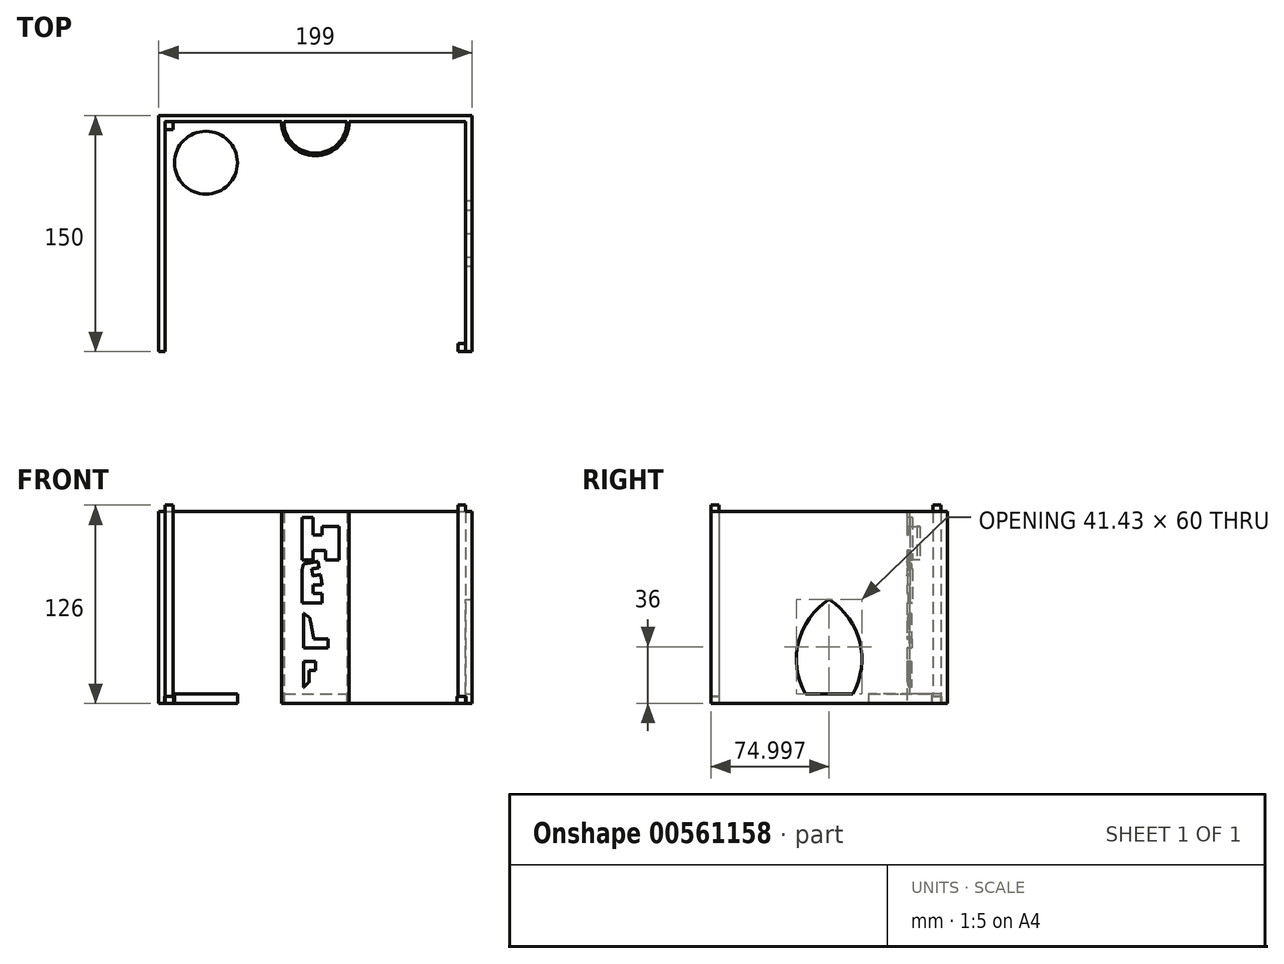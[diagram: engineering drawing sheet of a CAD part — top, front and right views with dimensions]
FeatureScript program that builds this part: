
annotation { "Feature Type Name" : "Feature", "Feature Type Description" : "" }
export const myFeature = defineFeature(function(context is Context, id is Id, definition is map)
    precondition{}
    {
        {
            var Q0;
            Q0=qCreatedBy(makeId("Top.planeOp"),FACE);
            var sketch = newSketch(context, id + "F0", { "sketchPlane" : qUnion([Q0])});
            skLineSegment(sketch, "E0.bottom", {"start": v(-131.47, 174.02) * mm, "end": v(-41.13, 174.02) * mm});
            skLineSegment(sketch, "E0.top", {"start": v(-131.47, 24.02) * mm, "end": v(-122.47, 24.02) * mm});
            skLineSegment(sketch, "E0.right", {"start": v(67.53, 174.02) * mm, "end": v(67.53, 24.02) * mm});
            skLineSegment(sketch, "E1", {"start": v(-131.47, 174.02) * mm, "end": v(-131.47, 24.02) * mm});
            skLineSegment(sketch, "E2.0", {"start": v(-127.47, 170.02) * mm, "end": v(-122.47, 170.02) * mm});
            skLineSegment(sketch, "E3.0", {"start": v(-127.47, 170.02) * mm, "end": v(-127.47, 24.02) * mm});
            skLineSegment(sketch, "E4.0", {"start": v(63.53, 170.02) * mm, "end": v(63.53, 24.02) * mm});
            skLineSegment(sketch, "E5", {"start": v(-19.6, 170.02) * mm, "end": v(63.53, 170.02) * mm});
            skLineSegment(sketch, "E6.top", {"start": v(-127.47, 165.02) * mm, "end": v(-122.47, 165.02) * mm});
            skLineSegment(sketch, "E6.left", {"start": v(-127.47, 170.02) * mm, "end": v(-127.47, 165.02) * mm});
            skLineSegment(sketch, "E6.right", {"start": v(-122.47, 170.02) * mm, "end": v(-122.47, 165.02) * mm});
            skLineSegment(sketch, "E7.bottom", {"start": v(63.53, 170.02) * mm, "end": v(58.53, 170.02) * mm});
            skLineSegment(sketch, "E7.top", {"start": v(63.53, 165.02) * mm, "end": v(58.53, 165.02) * mm});
            skLineSegment(sketch, "E7.left", {"start": v(63.53, 170.02) * mm, "end": v(63.53, 165.02) * mm});
            skLineSegment(sketch, "E7.right", {"start": v(58.53, 170.02) * mm, "end": v(58.53, 165.02) * mm});
            skLineSegment(sketch, "E8.bottom", {"start": v(-127.47, 24.02) * mm, "end": v(-122.47, 24.02) * mm});
            skLineSegment(sketch, "E8.top", {"start": v(-127.47, 29.02) * mm, "end": v(-122.47, 29.02) * mm});
            skLineSegment(sketch, "E8.left", {"start": v(-127.47, 24.02) * mm, "end": v(-127.47, 29.02) * mm});
            skLineSegment(sketch, "E8.right", {"start": v(-122.47, 24.02) * mm, "end": v(-122.47, 29.02) * mm});
            skLineSegment(sketch, "E9.bottom", {"start": v(63.53, 24.02) * mm, "end": v(58.53, 24.02) * mm});
            skLineSegment(sketch, "E9.top", {"start": v(63.53, 29.02) * mm, "end": v(58.53, 29.02) * mm});
            skLineSegment(sketch, "E9.left", {"start": v(63.53, 24.02) * mm, "end": v(63.53, 29.02) * mm});
            skLineSegment(sketch, "E9.right", {"start": v(58.53, 24.02) * mm, "end": v(58.53, 29.02) * mm});
            skPoint(sketch, "E10.centerSnap0", {"position": v(-31.97, 174.02) * mm});
            skLineSegment(sketch, "E11.trimOffspring", {"start": v(-22.8, 174.02) * mm, "end": v(67.53, 174.02) * mm});
            skLineSegment(sketch, "E12.trimOffspring", {"start": v(-21.97, 170.02) * mm, "end": v(-19.6, 170.02) * mm});
            skLineSegment(sketch, "E13", {"start": v(-21.97, 170.02) * mm, "end": v(-122.47, 170.02) * mm});
            skLineSegment(sketch, "E14", {"start": v(-41.13, 174.02) * mm, "end": v(-22.8, 174.02) * mm});
            skPoint(sketch, "E10.center.orphan", {"position": v(-31.97, 170.02) * mm});
            skArc(sketch, "E15", {"start": v(-51.97, 170.02) * mm, "mid": v(-31.97, 150.02) * mm, "end": v(-11.97, 170.02) * mm});
            skArc(sketch, "E16", {"start": v(-53.47, 170.02) * mm, "mid": v(-31.97, 148.52) * mm, "end": v(-10.47, 170.02) * mm});
            skLineSegment(sketch, "E17.trimOffspring", {"start": v(58.53, 24.02) * mm, "end": v(67.53, 24.02) * mm});
            skSolve(sketch);
        }
        {
            var Q0;
            Q0=makeQuery(id+"F0.imprint","IMPRINT",FACE,{"disambiguationData":[TD([[makeQuery(id+"F0.imprint","IMPRINT",EDGE,{"derivedFrom":sQuery(id+"F0.wireOp",EDGE,"E0.bottom")}),-1.0]])]});
            var Q1;
            {var subQ0=sQuery(id+"F0.wireOp",EDGE,"E15");Q1=makeQuery(id+"F0.imprint","IMPRINT",FACE,{"disambiguationData":[TD([[makeQuery(id+"F0.imprint","IMPRINT",EDGE,{"derivedFrom":subQ0}),-1.0]])]});}
            extrude(context, id + "F1", {"entities" : qUnion([Q0, Q1]), "depth" : 122 * mm, "offsetDistance" : 25 * mm});
        }
        {
            var Q0;
            Q0=makeQuery(id+"F0.imprint","IMPRINT",FACE,{"disambiguationData":[TD([[makeQuery(id+"F0.imprint","IMPRINT",EDGE,{"derivedFrom":sQuery(id+"F0.wireOp",EDGE,"E2.0")}),-1.0]])]});
            var Q1;
            Q1=makeQuery(id+"F0.imprint","IMPRINT",FACE,{"disambiguationData":[TD([[makeQuery(id+"F0.imprint","IMPRINT",EDGE,{"derivedFrom":sQuery(id+"F0.wireOp",EDGE,"E7.bottom")}),1.0]])]});
            var Q2;
            Q2=makeQuery(id+"F0.imprint","IMPRINT",FACE,{"disambiguationData":[TD([[makeQuery(id+"F0.imprint","IMPRINT",EDGE,{"derivedFrom":sQuery(id+"F0.wireOp",EDGE,"E9.top")}),1.0]])]});
            var Q3;
            Q3=makeQuery(id+"F0.imprint","IMPRINT",FACE,{"disambiguationData":[TD([[makeQuery(id+"F0.imprint","IMPRINT",EDGE,{"derivedFrom":sQuery(id+"F0.wireOp",EDGE,"E8.bottom")}),1.0]])]});
            extrude(context, id + "F2", {"entities" : qUnion([Q0, Q1, Q2, Q3]), "operationType" : NewBodyOperationType.ADD, "depth" : 126 * mm, "offsetDistance" : 25 * mm});
        }
        {
            var Q0;
            Q0=makeQuery(id+"F0.imprint","IMPRINT",FACE,{"disambiguationData":[TD([[makeQuery(id+"F0.imprint","IMPRINT",EDGE,{"derivedFrom":sQuery(id+"F0.wireOp",EDGE,"E0.bottom")}),-1.0]])]});
            var sketch = newSketch(context, id + "F3", { "sketchPlane" : qUnion([Q0])});
            skLineSegment(sketch, "E18.bottom", {"start": v(67.54, 24.02) * mm, "end": v(-131.47, 24.02) * mm});
            skLineSegment(sketch, "E18.top", {"start": v(67.54, 174.02) * mm, "end": v(-131.47, 174.02) * mm});
            skLineSegment(sketch, "E18.left", {"start": v(67.54, 24.02) * mm, "end": v(67.54, 174.02) * mm});
            skLineSegment(sketch, "E18.right", {"start": v(-131.47, 24.02) * mm, "end": v(-131.47, 174.02) * mm});
            skLineSegment(sketch, "E19", {"start": v(-131.47, 174.02) * mm, "end": v(-101.47, 174.02) * mm});
            skCircle(sketch, "E20", {"center": v(-101.47, 144.02) * mm, "radius": 20 * mm});
            skLineSegment(sketch, "E21", {"start": v(-51.96, 170.02) * mm, "end": v(-11.96, 170.02) * mm});
            skArc(sketch, "E22", {"start": v(-51.96, 170.02) * mm, "mid": v(-31.96, 150.02) * mm, "end": v(-11.96, 170.02) * mm});
            skSolve(sketch);
        }
        {
            var Q0;
            Q0 = qSketchRegion(id + "F3", true);
            extrude(context, id + "F4", {"entities" : qUnion([Q0]), "operationType" : NewBodyOperationType.ADD, "depth" : 6 * mm, "offsetDistance" : 25 * mm});
        }
        {
            var Q0;
            Q0=makeQuery(id+"F1.opExtrude","SWEPT_FACE",FACE,{"disambiguationData":[OSD([sQuery(id+"F0.wireOp",EDGE,"E0.right")])]});
            var sketch = newSketch(context, id + "F5", { "sketchPlane" : qUnion([Q0])});
            skPoint(sketch, "E23.endSnap0", {"position": v(99.02, 0) * mm});
            skLineSegment(sketch, "E24", {"start": v(99.02, 6) * mm, "end": v(114.02, 6) * mm});
            skLineSegment(sketch, "E25.MirrorCS", {"start": v(99.02, 6) * mm, "end": v(84.02, 6) * mm});
            skArc(sketch, "E26", {"start": v(114.02, 6) * mm, "mid": v(118.46, 38.99) * mm, "end": v(99.02, 66) * mm});
            skArc(sketch, "E27.MirrorCS", {"start": v(84.02, 6) * mm, "mid": v(79.58, 38.99) * mm, "end": v(99.02, 66) * mm});
            skPoint(sketch, "E23.start.orphan", {"position": v(99.02, 0) * mm});
            skSolve(sketch);
        }
        {
            var Q0;
            Q0=makeQuery(id+"F5.imprint","IMPRINT",FACE,{"disambiguationData":[TD([[makeQuery(id+"F5.imprint","IMPRINT",EDGE,{"derivedFrom":sQuery(id+"F5.wireOp",EDGE,"E24")}),1.0]])]});
            extrude(context, id + "F6", {"entities" : qUnion([Q0]), "operationType" : NewBodyOperationType.REMOVE, "oppositeDirection" : true, "depth" : 4 * mm, "offsetDistance" : 25 * mm});
        }
        {
            var Q0;
            {var subQ0=sQuery(id+"F0.wireOp",EDGE,"E17.trimOffspring");var subQ1=sQuery(id+"F0.wireOp",EDGE,"E9.left");var subQ2=sQuery(id+"F0.wireOp",EDGE,"E8.left");var subQ3=sQuery(id+"F0.wireOp",EDGE,"E7.left");var subQ4=sQuery(id+"F0.wireOp",EDGE,"E7.bottom");var subQ5=sQuery(id+"F0.wireOp",EDGE,"E6.left");var subQ6=sQuery(id+"F0.wireOp",EDGE,"E2.0");Q0=makeQuery(id+"F4.boolean.opBoolean","MERGE",FACE,{"derivedFrom":[makeQuery(id+"F2.boolean.opBoolean","MERGE",FACE,{"derivedFrom":[makeQuery(id+"F1.opExtrude","CAP_FACE",FACE,{"disambiguationData":[OSD([sQuery(id+"F0.wireOp",EDGE,"E0.bottom"),sQuery(id+"F0.wireOp",EDGE,"E0.top"),sQuery(id+"F0.wireOp",EDGE,"E0.right"),sQuery(id+"F0.wireOp",EDGE,"E1"),sQuery(id+"F0.wireOp",EDGE,"E3.0"),sQuery(id+"F0.wireOp",EDGE,"E4.0"),sQuery(id+"F0.wireOp",EDGE,"E5"),subQ6,subQ5,subQ4,subQ3,subQ2,subQ1,sQuery(id+"F0.wireOp",EDGE,"E11.trimOffspring"),sQuery(id+"F0.wireOp",EDGE,"E12.trimOffspring"),sQuery(id+"F0.wireOp",EDGE,"E13"),sQuery(id+"F0.wireOp",EDGE,"E14"),sQuery(id+"F0.wireOp",EDGE,"E15"),sQuery(id+"F0.wireOp",EDGE,"E16"),subQ0])],"isStart":true}),makeQuery(id+"F2.opExtrude","CAP_FACE",FACE,{"disambiguationData":[OSD([subQ6,sQuery(id+"F0.wireOp",EDGE,"E6.top"),subQ5,sQuery(id+"F0.wireOp",EDGE,"E6.right")])],"isStart":true}),makeQuery(id+"F2.opExtrude","CAP_FACE",FACE,{"disambiguationData":[OSD([subQ4,sQuery(id+"F0.wireOp",EDGE,"E7.top"),subQ3,sQuery(id+"F0.wireOp",EDGE,"E7.right")])],"isStart":true}),makeQuery(id+"F2.opExtrude","CAP_FACE",FACE,{"disambiguationData":[OSD([sQuery(id+"F0.wireOp",EDGE,"E8.bottom"),sQuery(id+"F0.wireOp",EDGE,"E8.top"),subQ2,sQuery(id+"F0.wireOp",EDGE,"E8.right")])],"isStart":true}),makeQuery(id+"F2.opExtrude","CAP_FACE",FACE,{"disambiguationData":[OSD([sQuery(id+"F0.wireOp",EDGE,"E9.top"),subQ1,sQuery(id+"F0.wireOp",EDGE,"E9.right"),subQ0])],"isStart":true})]}),makeQuery(id+"F4.opExtrude","CAP_FACE",FACE,{"disambiguationData":[OSD([sQuery(id+"F3.wireOp",EDGE,"E18.bottom"),sQuery(id+"F3.wireOp",EDGE,"E18.top"),sQuery(id+"F3.wireOp",EDGE,"E18.left"),sQuery(id+"F3.wireOp",EDGE,"E18.right"),sQuery(id+"F3.wireOp",EDGE,"E19"),sQuery(id+"F3.wireOp",EDGE,"E20"),sQuery(id+"F3.wireOp",EDGE,"E21"),sQuery(id+"F3.wireOp",EDGE,"E22")])],"isStart":true})]});}
            var sketch = newSketch(context, id + "F7", { "sketchPlane" : qUnion([Q0])});
            skLineSegment(sketch, "E28.bottom", {"start": v(-127.47, -24.02) * mm, "end": v(-122.19, -24.02) * mm});
            skLineSegment(sketch, "E29", {"start": v(-127.72, -24.02) * mm, "end": v(-127.72, -29.32) * mm});
            skLineSegment(sketch, "E30", {"start": v(-127.72, -29.32) * mm, "end": v(-122.19, -29.32) * mm});
            skLineSegment(sketch, "E31", {"start": v(-122.19, -29.32) * mm, "end": v(-122.19, -24.02) * mm});
            skLineSegment(sketch, "E32.bottom", {"start": v(58.53, -24.02) * mm, "end": v(58.28, -24.02) * mm});
            skLineSegment(sketch, "E33.top", {"start": v(58.28, -29.23) * mm, "end": v(63.85, -29.23) * mm});
            skLineSegment(sketch, "E33.left", {"start": v(58.28, -24.02) * mm, "end": v(58.28, -29.23) * mm});
            skLineSegment(sketch, "E33.right", {"start": v(63.85, -24.02) * mm, "end": v(63.85, -29.23) * mm});
            skLineSegment(sketch, "E34.top", {"start": v(63.54, -170.26) * mm, "end": v(63.78, -170.26) * mm});
            skLineSegment(sketch, "E34.right", {"start": v(63.78, -170.02) * mm, "end": v(63.78, -170.26) * mm});
            skLineSegment(sketch, "E35.bottom", {"start": v(63.78, -170.26) * mm, "end": v(58.1, -170.26) * mm});
            skLineSegment(sketch, "E35.top", {"start": v(63.78, -164.76) * mm, "end": v(58.1, -164.76) * mm});
            skLineSegment(sketch, "E35.left", {"start": v(63.78, -170.26) * mm, "end": v(63.78, -164.76) * mm});
            skLineSegment(sketch, "E35.right", {"start": v(58.1, -170.26) * mm, "end": v(58.1, -164.76) * mm});
            skLineSegment(sketch, "E36.top", {"start": v(-127.46, -170.3) * mm, "end": v(-127.71, -170.3) * mm});
            skLineSegment(sketch, "E36.right", {"start": v(-127.71, -170.02) * mm, "end": v(-127.71, -170.3) * mm});
            skLineSegment(sketch, "E37.bottom", {"start": v(-127.71, -170.3) * mm, "end": v(-121.95, -170.3) * mm});
            skLineSegment(sketch, "E37.top", {"start": v(-127.71, -164.76) * mm, "end": v(-121.95, -164.76) * mm});
            skLineSegment(sketch, "E37.left", {"start": v(-127.71, -170.3) * mm, "end": v(-127.71, -164.76) * mm});
            skLineSegment(sketch, "E37.right", {"start": v(-121.95, -170.3) * mm, "end": v(-121.95, -164.76) * mm});
            skLineSegment(sketch, "E38", {"start": v(58.28, -24.02) * mm, "end": v(63.85, -24.02) * mm});
            skPoint(sketch, "E39.orphan", {"position": v(-122.19, -23.76) * mm});
            skLineSegment(sketch, "E40", {"start": v(-127.47, -24.02) * mm, "end": v(-127.72, -24.02) * mm});
            skPoint(sketch, "E41.end.orphan", {"position": v(-127.47, -23.76) * mm});
            skSolve(sketch);
        }
        {
            var Q0;
            Q0 = qSketchRegion(id + "F7", true);
            extrude(context, id + "F8", {"entities" : qUnion([Q0]), "operationType" : NewBodyOperationType.REMOVE, "oppositeDirection" : true, "depth" : 4.5 * mm, "offsetDistance" : 25 * mm});
        }
        {
            var Q0;
            Q0=qCreatedBy(makeId("Front.planeOp"),FACE);
            var sketch = newSketch(context, id + "F9", { "sketchPlane" : qUnion([Q0])});
            skLineSegment(sketch, "E42", {"start": v(-40.33, 105.44) * mm, "end": v(-40.33, 91.16) * mm});
            skLineSegment(sketch, "E43", {"start": v(-40.33, 91.16) * mm, "end": v(-33.59, 91.16) * mm});
            skLineSegment(sketch, "E44", {"start": v(-33.59, 91.16) * mm, "end": v(-33.59, 97.1) * mm});
            skLineSegment(sketch, "E45", {"start": v(-33.59, 97.1) * mm, "end": v(-25.65, 97.1) * mm});
            skLineSegment(sketch, "E46", {"start": v(-25.65, 97.1) * mm, "end": v(-25.65, 91.16) * mm});
            skLineSegment(sketch, "E47", {"start": v(-25.65, 91.16) * mm, "end": v(-16.93, 91.16) * mm});
            skLineSegment(sketch, "E48", {"start": v(-16.93, 91.16) * mm, "end": v(-16.93, 112.58) * mm});
            skLineSegment(sketch, "E49", {"start": v(-16.93, 112.58) * mm, "end": v(-27.64, 112.58) * mm});
            skLineSegment(sketch, "E50", {"start": v(-27.64, 112.58) * mm, "end": v(-27.64, 107.02) * mm});
            skLineSegment(sketch, "E51", {"start": v(-27.64, 107.02) * mm, "end": v(-33.59, 107.02) * mm});
            skLineSegment(sketch, "E52", {"start": v(-33.59, 107.02) * mm, "end": v(-33.59, 118.13) * mm});
            skLineSegment(sketch, "E53", {"start": v(-33.59, 118.13) * mm, "end": v(-40.33, 118.13) * mm});
            skLineSegment(sketch, "E54", {"start": v(-40.33, 118.13) * mm, "end": v(-40.33, 105.44) * mm});
            skLineSegment(sketch, "E55", {"start": v(-40.33, 80.05) * mm, "end": v(-40.33, 63.78) * mm});
            skLineSegment(sketch, "E56", {"start": v(-40.33, 63.78) * mm, "end": v(-27.64, 63.78) * mm});
            skLineSegment(sketch, "E57", {"start": v(-27.64, 63.78) * mm, "end": v(-27.64, 69.73) * mm});
            skLineSegment(sketch, "E58", {"start": v(-27.64, 69.73) * mm, "end": v(-33.59, 69.73) * mm});
            skLineSegment(sketch, "E59", {"start": v(-33.59, 69.73) * mm, "end": v(-33.59, 75.29) * mm});
            skLineSegment(sketch, "E60", {"start": v(-33.59, 75.29) * mm, "end": v(-27.64, 75.29) * mm});
            skLineSegment(sketch, "E61", {"start": v(-27.64, 75.29) * mm, "end": v(-28.7, 81.86) * mm});
            skLineSegment(sketch, "E62", {"start": v(-28.7, 81.86) * mm, "end": v(-33.59, 81.06) * mm});
            skLineSegment(sketch, "E63", {"start": v(-33.59, 81.06) * mm, "end": v(-34.3, 85.45) * mm});
            skLineSegment(sketch, "E64", {"start": v(-40.33, 85.45) * mm, "end": v(-40.33, 80.05) * mm});
            skLineSegment(sketch, "E65", {"start": v(-34.3, 85.45) * mm, "end": v(-29.65, 86.2) * mm});
            skLineSegment(sketch, "E66", {"start": v(-29.65, 86.2) * mm, "end": v(-30.3, 90.2) * mm});
            skLineSegment(sketch, "E67", {"start": v(-30.3, 90.2) * mm, "end": v(-39.45, 88.71) * mm});
            skLineSegment(sketch, "E68", {"start": v(-39.45, 88.71) * mm, "end": v(-40.33, 85.45) * mm});
            skLineSegment(sketch, "E69", {"start": v(-39.44, 57.25) * mm, "end": v(-39.44, 35.37) * mm});
            skLineSegment(sketch, "E70", {"start": v(-39.44, 35.37) * mm, "end": v(-24.01, 35.37) * mm});
            skLineSegment(sketch, "E71", {"start": v(-24.01, 35.37) * mm, "end": v(-24.01, 40.98) * mm});
            skLineSegment(sketch, "E72", {"start": v(-24.01, 40.98) * mm, "end": v(-33, 40.98) * mm});
            skLineSegment(sketch, "E73", {"start": v(-33, 40.98) * mm, "end": v(-35.52, 54.45) * mm});
            skLineSegment(sketch, "E74", {"start": v(-35.52, 54.45) * mm, "end": v(-39.44, 57.25) * mm});
            skLineSegment(sketch, "E75", {"start": v(-39.44, 26.67) * mm, "end": v(-39.44, 11.53) * mm});
            skLineSegment(sketch, "E76", {"start": v(-39.44, 26.67) * mm, "end": v(-31.87, 26.67) * mm});
            skLineSegment(sketch, "E77", {"start": v(-31.87, 26.67) * mm, "end": v(-31.87, 21.06) * mm});
            skLineSegment(sketch, "E78", {"start": v(-31.87, 21.06) * mm, "end": v(-36.08, 21.06) * mm});
            skLineSegment(sketch, "E79", {"start": v(-36.08, 21.06) * mm, "end": v(-36.08, 13.5) * mm});
            skLineSegment(sketch, "E80", {"start": v(-36.08, 13.5) * mm, "end": v(-39.44, 10.12) * mm});
            skLineSegment(sketch, "E81", {"start": v(-39.44, 11.53) * mm, "end": v(-39.44, 10.12) * mm});
            skSolve(sketch);
        }
        {
            var Q0;
            Q0=makeQuery(id+"F9.imprint","IMPRINT",FACE,{"disambiguationData":[TD([[makeQuery(id+"F9.imprint","IMPRINT",EDGE,{"derivedFrom":sQuery(id+"F9.wireOp",EDGE,"E42")}),1.0]])]});
            var Q1;
            Q1=makeQuery(id+"F9.imprint","IMPRINT",FACE,{"disambiguationData":[TD([[makeQuery(id+"F9.imprint","IMPRINT",EDGE,{"derivedFrom":sQuery(id+"F9.wireOp",EDGE,"E55")}),1.0]])]});
            var Q2;
            Q2=makeQuery(id+"F9.imprint","IMPRINT",FACE,{"disambiguationData":[TD([[makeQuery(id+"F9.imprint","IMPRINT",EDGE,{"derivedFrom":sQuery(id+"F9.wireOp",EDGE,"E69")}),1.0]])]});
            var Q3;
            Q3=makeQuery(id+"F9.imprint","IMPRINT",FACE,{"disambiguationData":[TD([[makeQuery(id+"F9.imprint","IMPRINT",EDGE,{"derivedFrom":sQuery(id+"F9.wireOp",EDGE,"E75")}),1.0]])]});
            extrude(context, id + "F10", {"entities" : qUnion([Q0, Q1, Q2, Q3]), "operationType" : NewBodyOperationType.REMOVE, "oppositeDirection" : true, "depth" : 158 * mm, "offsetDistance" : 25 * mm});
        }
    });
